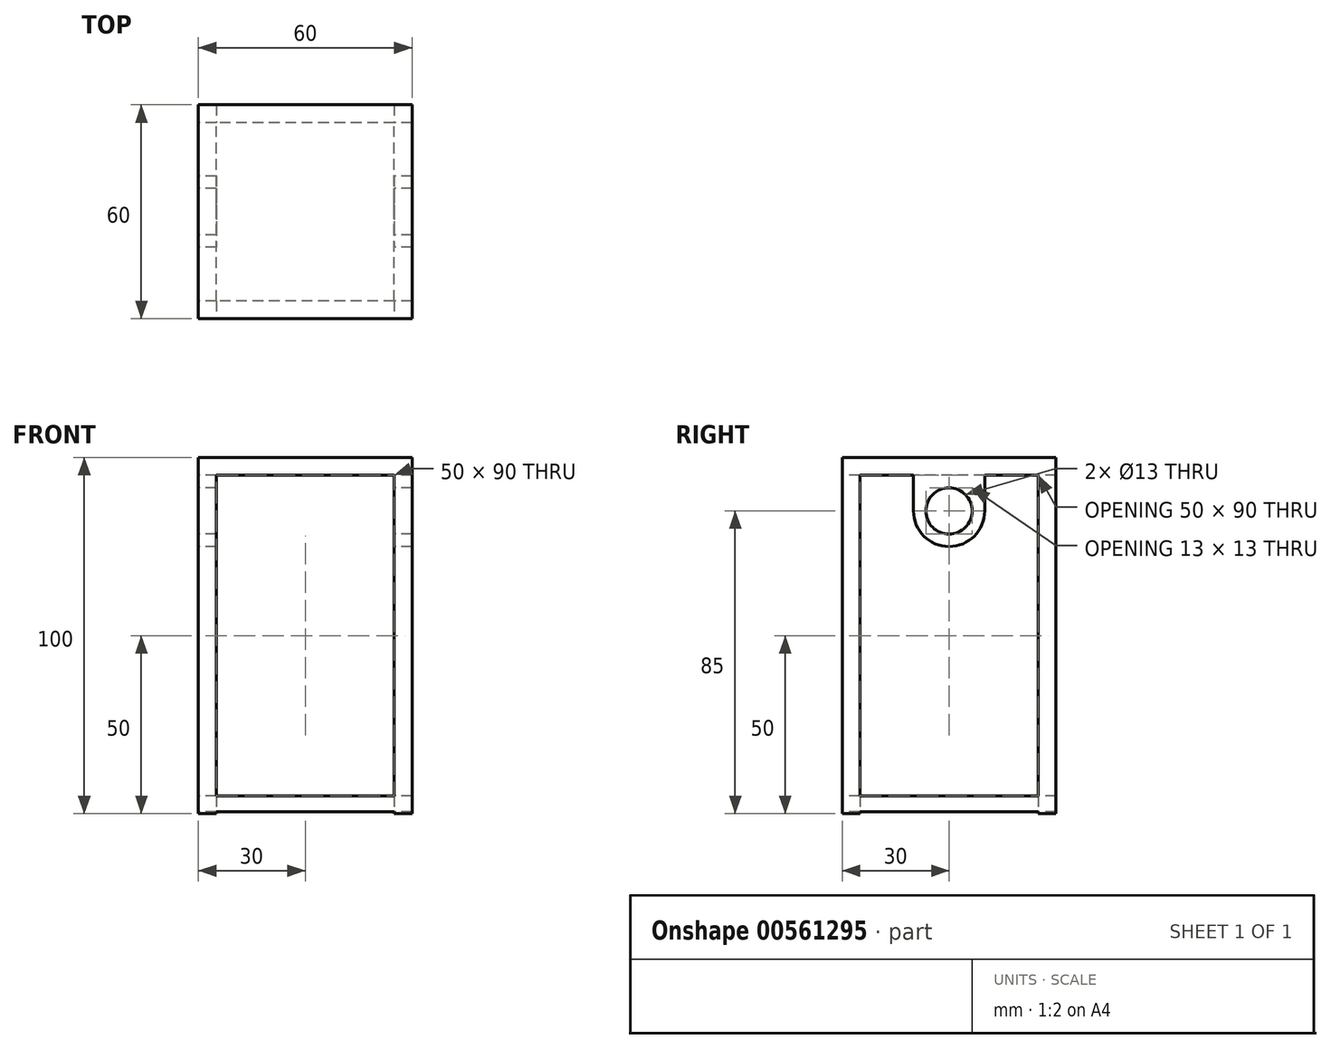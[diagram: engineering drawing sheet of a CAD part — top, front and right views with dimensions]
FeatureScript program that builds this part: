
annotation { "Feature Type Name" : "Feature", "Feature Type Description" : "" }
export const myFeature = defineFeature(function(context is Context, id is Id, definition is map)
    precondition{}
    {
        {
            var Q0;
            Q0=qCreatedBy(makeId("Right.planeOp"),FACE);
            var sketch = newSketch(context, id + "F0", { "sketchPlane" : qUnion([Q0])});
            skLineSegment(sketch, "E0.bottom", {"start": v(-55, 90) * mm, "end": v(5, 90) * mm});
            skLineSegment(sketch, "E0.top", {"start": v(-55, 95) * mm, "end": v(5, 95) * mm});
            skLineSegment(sketch, "E0.left", {"start": v(-55, 90) * mm, "end": v(-55, 95) * mm});
            skLineSegment(sketch, "E0.right", {"start": v(5, 90) * mm, "end": v(5, 95) * mm});
            skCircle(sketch, "E1", {"center": v(-25, 80) * mm, "radius": 10 * mm});
            skPoint(sketch, "E1.centerSnap0", {"position": v(-25, 90) * mm});
            skLineSegment(sketch, "E2", {"start": v(-35, 80) * mm, "end": v(-35, 90) * mm});
            skLineSegment(sketch, "E3", {"start": v(-35, 90) * mm, "end": v(-15, 90) * mm});
            skLineSegment(sketch, "E4", {"start": v(-15, 90) * mm, "end": v(-15, 80) * mm});
            skLineSegment(sketch, "E5.bottom", {"start": v(-55, 90) * mm, "end": v(-50, 90) * mm});
            skLineSegment(sketch, "E5.top", {"start": v(-55, -5) * mm, "end": v(-50, -5) * mm});
            skLineSegment(sketch, "E5.left", {"start": v(-55, 90) * mm, "end": v(-55, -5) * mm});
            skLineSegment(sketch, "E5.right", {"start": v(-50, 90) * mm, "end": v(-50, -5) * mm});
            skLineSegment(sketch, "E6.bottom", {"start": v(5, 90) * mm, "end": v(0, 90) * mm});
            skLineSegment(sketch, "E6.top", {"start": v(5, -5) * mm, "end": v(0, -5) * mm});
            skLineSegment(sketch, "E6.left", {"start": v(5, 90) * mm, "end": v(5, -5) * mm});
            skLineSegment(sketch, "E6.right", {"start": v(0, 90) * mm, "end": v(0, -5) * mm});
            skCircle(sketch, "E7", {"center": v(-25, 80) * mm, "radius": 6.5 * mm});
            skLineSegment(sketch, "E8.top", {"start": v(-50, 0) * mm, "end": v(0, 0) * mm});
            skLineSegment(sketch, "E8.left", {"start": v(-50, -5) * mm, "end": v(-50, 0) * mm});
            skLineSegment(sketch, "E8.right", {"start": v(0, -4.5) * mm, "end": v(0, 0) * mm});
            skLineSegment(sketch, "E9", {"start": v(-50, -4.5) * mm, "end": v(0, -4.5) * mm});
            skSolve(sketch);
        }
        {
            var Q0;
            Q0 = qSketchRegion(id + "F0", true);
            var Q1;
            Q1=makeQuery(id+"F0.imprint","IMPRINT",FACE,{"disambiguationData":[TD([[makeQuery(id+"F0.imprint","IMPRINT",EDGE,{"derivedFrom":sQuery(id+"F0.wireOp",EDGE,"E7")}),-1.0]])]});
            var Q2;
            {var subQ0=sQuery(id+"F0.wireOp",EDGE,"E2");Q2=makeQuery(id+"F0.imprint","IMPRINT",FACE,{"disambiguationData":[TD([[makeQuery(id+"F0.imprint","IMPRINT",EDGE,{"derivedFrom":subQ0}),-1.0]])]});}
            var Q3;
            {var subQ0=sQuery(id+"F0.wireOp",EDGE,"E4");Q3=makeQuery(id+"F0.imprint","IMPRINT",FACE,{"disambiguationData":[TD([[makeQuery(id+"F0.imprint","IMPRINT",EDGE,{"derivedFrom":subQ0}),-1.0]])]});}
            extrude(context, id + "F1", {"entities" : qUnion([Q0, Q1, Q2, Q3]), "depth" : 60 * mm, "offsetDistance" : 25 * mm});
        }
        {
            var Q0;
            Q0=makeQuery(id+"F1.opExtrude","SWEPT_FACE",FACE,{"disambiguationData":[OSD([sQuery(id+"F0.wireOp",EDGE,"E0.left"),sQuery(id+"F0.wireOp",EDGE,"E5.left")])]});
            cPlane(context, id + "F2", {"entities" : qUnion([Q0]), "cplaneType" : CPlaneType.OFFSET, "offset" : 0 * mm, "width" : 150 * mm, "height" : 150 * mm});
        }
        {
            var Q0;
            Q0=makeQuery(id+"FBcqFYk5EqDwSJQ_1.boolean.opBoolean","MERGE",FACE,{"derivedFrom":[makeQuery(id+"F1.opExtrude","SWEPT_FACE",FACE,{"disambiguationData":[OSD([sQuery(id+"F0.wireOp",EDGE,"E9")])]}),makeQuery(id+"FBcqFYk5EqDwSJQ_1.opExtrude","SWEPT_FACE",FACE,{"disambiguationData":[OSD([sQuery(id+"F4R80SfL9nQv767_1.wireOp",EDGE,"hQHxdW2Z-Ecps-ILFM-gth5-rHAedAXdPAFl.bottom")])]})]});
            cPlane(context, id + "F3", {"entities" : qUnion([Q0]), "cplaneType" : CPlaneType.OFFSET, "offset" : 0 * mm, "width" : 150 * mm, "height" : 150 * mm});
        }
        {
            var Q0;
            Q0=qCreatedBy(id+"F3.planeOp",FACE);
            var sketch = newSketch(context, id + "F4", { "sketchPlane" : qUnion([Q0])});
            skLineSegment(sketch, "E10.bottom", {"start": v(5, 50) * mm, "end": v(55, 50) * mm});
            skLineSegment(sketch, "E10.top", {"start": v(5, 0) * mm, "end": v(55, 0) * mm});
            skLineSegment(sketch, "E10.left", {"start": v(5, 50) * mm, "end": v(5, 0) * mm});
            skLineSegment(sketch, "E10.right", {"start": v(55, 50) * mm, "end": v(55, 0) * mm});
            skSolve(sketch);
        }
        {
            var Q0;
            Q0 = qSketchRegion(id + "F4", true);
            extrude(context, id + "F5", {"entities" : qUnion([Q0]), "operationType" : NewBodyOperationType.REMOVE, "oppositeDirection" : true, "depth" : 4.5 * mm, "offsetDistance" : 25 * mm});
        }
        {
            var Q0;
            Q0=qCreatedBy(id+"F2.planeOp",FACE);
            var sketch = newSketch(context, id + "F6", { "sketchPlane" : qUnion([Q0])});
            skLineSegment(sketch, "E11.bottom", {"start": v(5, 90) * mm, "end": v(55, 90) * mm});
            skLineSegment(sketch, "E11.top", {"start": v(5, 25) * mm, "end": v(55, 25) * mm});
            skLineSegment(sketch, "E11.left", {"start": v(5, 90) * mm, "end": v(5, 25) * mm});
            skLineSegment(sketch, "E11.right", {"start": v(55, 90) * mm, "end": v(55, 25) * mm});
            skLineSegment(sketch, "E12.left", {"start": v(5, 25) * mm, "end": v(5, 0) * mm});
            skLineSegment(sketch, "E12.right", {"start": v(55, 25) * mm, "end": v(55, 0) * mm});
            skLineSegment(sketch, "E13", {"start": v(5, 0) * mm, "end": v(55, 0) * mm});
            skLineSegment(sketch, "E14.bottom", {"start": v(5, -4.5) * mm, "end": v(55, -4.5) * mm});
            skLineSegment(sketch, "E14.top", {"start": v(5, -5) * mm, "end": v(55, -5) * mm});
            skLineSegment(sketch, "E14.left", {"start": v(5, -4.5) * mm, "end": v(5, -5) * mm});
            skLineSegment(sketch, "E14.right", {"start": v(55, -4.5) * mm, "end": v(55, -5) * mm});
            skSolve(sketch);
        }
        {
            var Q0;
            Q0 = qSketchRegion(id + "F6", true);
            extrude(context, id + "F7", {"entities" : qUnion([Q0]), "operationType" : NewBodyOperationType.REMOVE, "oppositeDirection" : true, "depth" : 60 * mm, "offsetDistance" : 25 * mm});
        }
    });
